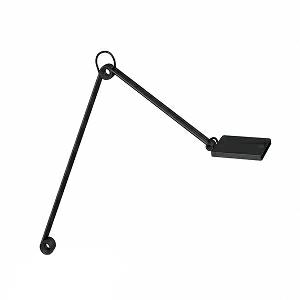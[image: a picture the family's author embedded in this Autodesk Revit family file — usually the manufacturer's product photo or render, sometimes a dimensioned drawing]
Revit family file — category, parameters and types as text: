
# Revit family: para_mi_-_ftl_108_r__940_00644091_9efb
name_source: partatom
category: Lighting Fixtures
units: mm (PartAtom-declared; Revit-internal decimal feet)

## family parameters
Cut with Voids When Loaded = No
Host = Face
Light Source = No
Part Type = Normal
Room Calculation Point = No
Round Connector Dimension = Use Diameter
Shared = No

## types (1)
- PARA.MI - FTL 108 R /940 (1 x LED, 600 lm, 4000K)
    Apparent Load = 7 VA
    Approval mark = CE
    CIE Flux Codes = 70 94 99 100 100
    Color Rendering = 90-100
    Color Temperature = 4000K
    Control Gear = Electronic ballast
    Default Elevation = 1800 mm
    Description = FTL 108 R|Task luminaire|light source: LED|work equipment: Electronic plug-in transformer|connected load: 100-240 V, 50/60 Hz|Power consumption: approx. 7 W|luminous flux: 600 lm|luminous efficacy: 85 lm/W|Illuminance efficiency factor: 111 lx/W|colour temperature: Cold white, ca. 4000 K|color rendering index (CRI): >= 90|chromaticity tolerance:  3 SDCM|class of protection: II with plug-in power supply, III without plug-in power supply|technology: Continuously dimmable|luminaire body|material: Aluminium|surface: Painted|colour: Black|lamp cover: Plastic, Clear|tubular sections|material: Tubular aluminium section|surface: Painted|colour: Jet black|weight (net): approx. 0.8 kg|mains lead: 3.00 m Mains plug BS 1363, CEE 7/XVI, NEMA 1-15P|Fastening: Adaptor (accessory), Table base (accessory), Table clamp (accessory), Tap16|glare control: Reflector|special features: Automatic switchoff adjustable, Push button in luminaire head, Behaviour at net recovery adjustable|Approval mark: C - ETL - US (F. CAN U. USA), VDE - ENEC SEP LIGHT & POWER SUPPLY UNIT|
    Height = 12 mm  [stored 0.0393701 ft]
    Lamp = 1 x LED
    Lamp Light Flux = 600 lm
    Lamp count = 1
    Length = 123 mm
    Luminous efficacy = 86 lm/W
    Manufacturer = Waldmann
    ModVariant = No
    Model = 00644091
    Mounting Place = Table
    Mounting Type = Surface mounted
    Number of Poles = 1
    OnlyDefault = Yes
    Power Factor = 1
    Product Name = PARA.MI - FTL 108 R /940
    Product group = Task luminaire (office)
    ProductGroupID = 21
    Protection Class = Protection class II
    Protection Degree = IP 40
    RLX_Detail_Level = 1
    RLX_Emergency_Light_Flux = 0 lm
    RLX_Emergency_Type = 0
    RLX_Emergency_Type_DB = No
    RlxData = <blob elided: 96657 chars, md5=2c6b65ec>
    Socket = socket
    Standby Power = 0 W
    System Light Flux = 600 lm
    System Power = 7 W
    Type Comments = Product without accessories
    Type Image = 113148000-00644091.jpg
    URL = http://relux.com
    VarID = ---
    Voltage = 230 V
    Voltage Range = 220-240 V
    Weight = 0.00 kg
    Width = 0 mm  [stored 0 ft]

note: [stored X ft] marks values corroborated as IEEE doubles in the binary element streams (Revit-internal decimal feet)

## geometry (parser evidence)
native form markers: Blend x4, Sweep x18
no freeform markers — native parametric forms only
